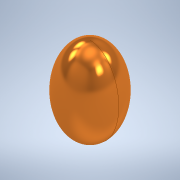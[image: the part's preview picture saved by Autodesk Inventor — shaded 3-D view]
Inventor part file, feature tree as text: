
AUTODESK INVENTOR PART (.ipt)
format: ipt  version: 2020 (Build 240168000, 168)  size: 232,448 bytes
history: native  units: mm
features: revolve x1, sketch x1
ambient origin geometry x8: Origin, YZ Plane, XZ Plane, XY Plane, X Axis, Y Axis, Z Axis, Center Point
bodies: Volumenkörper1 (feature_tree)
feature tree (2):
  revolve  "Umdrehung1"
  sketch  "Skizze2"  dims[d0=20.0mm d1=30.0mm d2=180.0deg]
